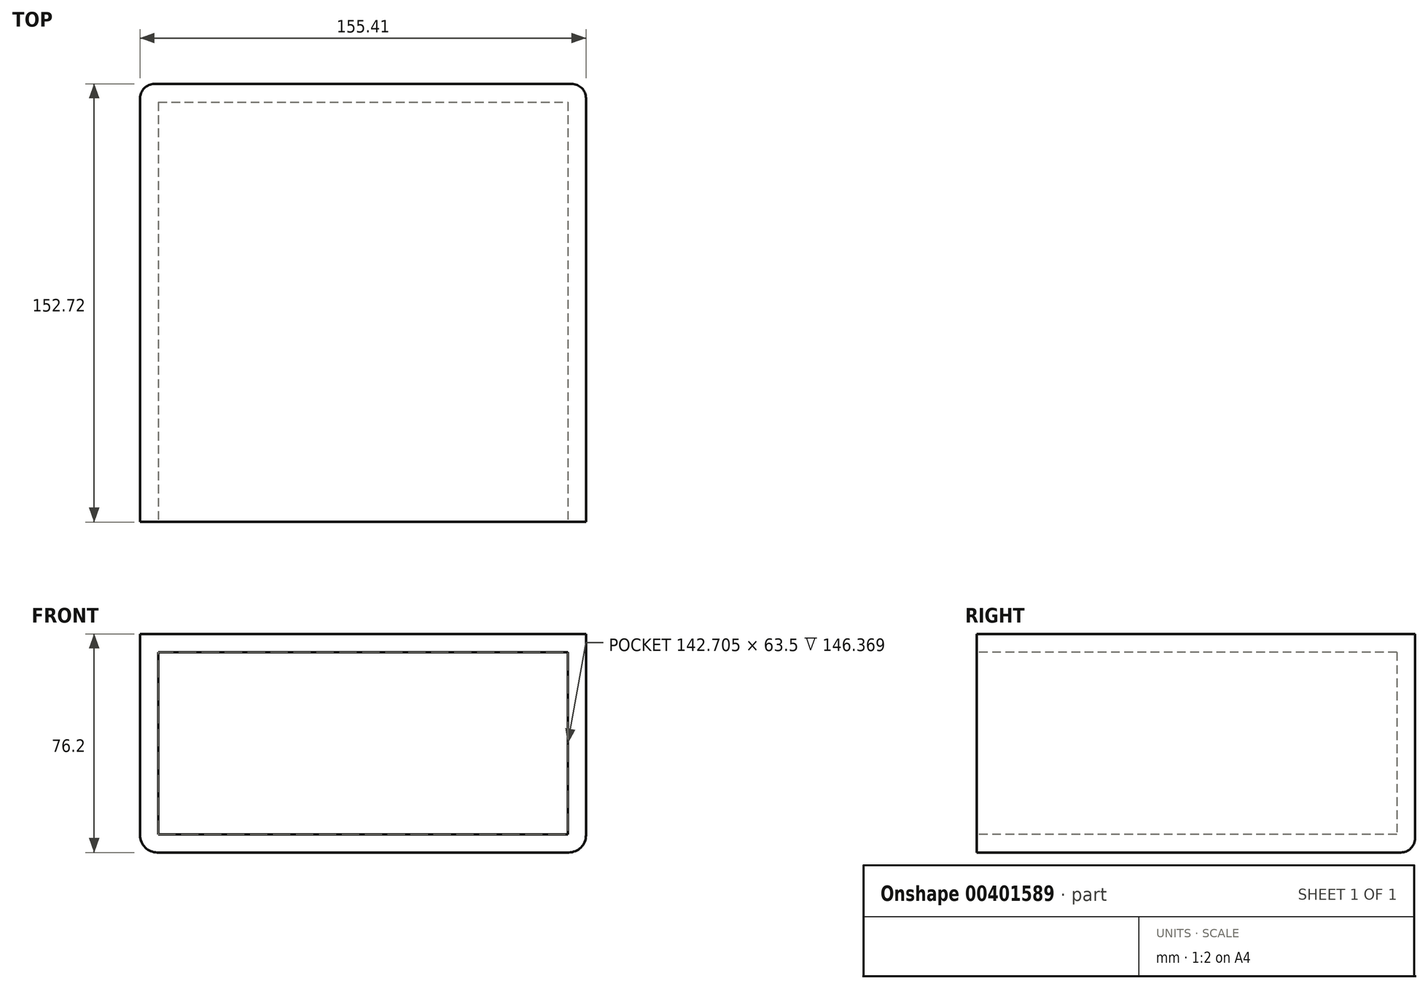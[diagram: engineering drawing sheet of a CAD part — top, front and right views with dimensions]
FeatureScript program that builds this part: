
annotation { "Feature Type Name" : "Feature", "Feature Type Description" : "" }
export const myFeature = defineFeature(function(context is Context, id is Id, definition is map)
    precondition{}
    {
        {
            var Q0;
            Q0=qCreatedBy(makeId("Top.planeOp"),FACE);
            var sketch = newSketch(context, id + "F0", { "sketchPlane" : qUnion([Q0])});
            skLineSegment(sketch, "E0.bottom", {"start": v(-79.4, 75.91) * mm, "end": v(76, 75.91) * mm});
            skLineSegment(sketch, "E0.top", {"start": v(-79.4, -76.8) * mm, "end": v(76, -76.8) * mm});
            skLineSegment(sketch, "E0.left", {"start": v(-79.4, 75.91) * mm, "end": v(-79.4, -76.8) * mm});
            skLineSegment(sketch, "E0.right", {"start": v(76, 75.91) * mm, "end": v(76, -76.8) * mm});
            skSolve(sketch);
        }
        {
            var Q0;
            Q0=makeQuery(id+"F0.imprint","IMPRINT",FACE,{"disambiguationData":[TD([[makeQuery(id+"F0.imprint","IMPRINT",EDGE,{"derivedFrom":sQuery(id+"F0.wireOp",EDGE,"E0.bottom")}),-1.0]])]});
            extrude(context, id + "F1", {"entities" : qUnion([Q0]), "depth" : 25.4 * mm});
        }
        {
            var Q0;
            Q0=makeQuery(id+"F1.opExtrude","CAP_FACE",FACE,{"disambiguationData":[OSD([sQuery(id+"F0.wireOp",EDGE,"E0.bottom"),sQuery(id+"F0.wireOp",EDGE,"E0.top"),sQuery(id+"F0.wireOp",EDGE,"E0.left"),sQuery(id+"F0.wireOp",EDGE,"E0.right")])],"isStart":false});
            extrude(context, id + "F2", {"entities" : qUnion([Q0]), "operationType" : NewBodyOperationType.ADD, "depth" : 25.4 * mm});
        }
        {
            var Q0;
            Q0=makeQuery(id+"F1.opExtrude","CAP_FACE",FACE,{"disambiguationData":[OSD([sQuery(id+"F0.wireOp",EDGE,"E0.bottom"),sQuery(id+"F0.wireOp",EDGE,"E0.top"),sQuery(id+"F0.wireOp",EDGE,"E0.left"),sQuery(id+"F0.wireOp",EDGE,"E0.right")])],"isStart":false});
            var Q1;
            Q1=makeQuery(id+"F1.opExtrude","CAP_FACE",FACE,{"disambiguationData":[OSD([sQuery(id+"F0.wireOp",EDGE,"E0.bottom"),sQuery(id+"F0.wireOp",EDGE,"E0.top"),sQuery(id+"F0.wireOp",EDGE,"E0.left"),sQuery(id+"F0.wireOp",EDGE,"E0.right")])],"isStart":true});
            extrude(context, id + "F3", {"entities" : qUnion([Q0, Q1]), "operationType" : NewBodyOperationType.ADD, "depth" : 25.4 * mm});
        }
        {
            var Q0;
            {var subQ0=sQuery(id+"F0.wireOp",EDGE,"E0.top");Q0=makeQuery(id+"F3.boolean.opBoolean","MERGE",FACE,{"derivedFrom":[makeQuery(id+"F1.opExtrude","SWEPT_FACE",FACE,{"disambiguationData":[OSD([subQ0])]}),makeQuery(id+"F3.opExtrude","SWEPT_FACE",FACE,{"disambiguationData":[OSD([subQ0]),TDD([makeQuery(id+"F1.opExtrude","CAP_EDGE",EDGE,{"disambiguationData":[OSD([subQ0])],"isStart":true})])]}),makeQuery(id+"F3.opExtrude","SWEPT_FACE",FACE,{"disambiguationData":[OSD([subQ0]),TDD([makeQuery(id+"F1.opExtrude","CAP_EDGE",EDGE,{"disambiguationData":[OSD([subQ0])],"isStart":false})])]})]});}
            shell(context, id + "F4", {"entities" : qUnion([Q0]), "thickness" : 6.35 * mm});
        }
        {
            var Q0;
            {var subQ0=sQuery(id+"F0.wireOp",EDGE,"E0.left");Q0=makeQuery(id+"F3.opExtrude","CAP_EDGE",EDGE,{"disambiguationData":[OSD([subQ0]),TDD([makeQuery(id+"F1.opExtrude","CAP_EDGE",EDGE,{"disambiguationData":[OSD([subQ0])],"isStart":false})])],"isStart":false});}
            var Q1;
            Q1=makeQuery(id+"F1.opExtrude","CAP_EDGE",EDGE,{"disambiguationData":[OSD([sQuery(id+"F0.wireOp",EDGE,"E0.left")])],"isStart":true});
            var Q2;
            {var subQ0=sQuery(id+"F0.wireOp",EDGE,"E0.right");Q2=makeQuery(id+"F3.opExtrude","CAP_EDGE",EDGE,{"disambiguationData":[OSD([subQ0]),TDD([makeQuery(id+"F1.opExtrude","CAP_EDGE",EDGE,{"disambiguationData":[OSD([subQ0])],"isStart":false})])],"isStart":false});}
            var Q3;
            Q3=makeQuery(id+"F1.opExtrude","CAP_EDGE",EDGE,{"disambiguationData":[OSD([sQuery(id+"F0.wireOp",EDGE,"E0.right")])],"isStart":true});
            fillet(context, id + "F5", {"entities" : qUnion([Q0, Q1, Q2, Q3]), "radius" : 6 * mm, "tangentPropagation" : true, "allowEdgeOverflow" : false});
        }
        {
            var Q0;
            {var subQ0=sQuery(id+"F0.wireOp",EDGE,"E0.bottom");Q0=makeQuery(id+"F3.opExtrude","CAP_EDGE",EDGE,{"disambiguationData":[OSD([subQ0]),TDD([makeQuery(id+"F1.opExtrude","CAP_EDGE",EDGE,{"disambiguationData":[OSD([subQ0])],"isStart":false})])],"isStart":false});}
            var Q1;
            {var subQ0=sQuery(id+"F0.wireOp",EDGE,"E0.left");var subQ1=sQuery(id+"F0.wireOp",EDGE,"E0.bottom");Q1=makeQuery(id+"F3.boolean.opBoolean","MERGE",EDGE,{"derivedFrom":[makeQuery(id+"F1.opExtrude","SWEPT_EDGE",EDGE,{"disambiguationData":[OSD([subQ1,subQ0])]}),makeQuery(id+"F3.opExtrude","SWEPT_EDGE",EDGE,{"disambiguationData":[OSD([subQ1,subQ0]),TDD([makeQuery(id+"F1.opExtrude","CAP_VERTEX",VERTEX,{"disambiguationData":[OSD([subQ1,subQ0])],"isStart":true})])]}),makeQuery(id+"F3.opExtrude","SWEPT_EDGE",EDGE,{"disambiguationData":[OSD([subQ1,subQ0]),TDD([makeQuery(id+"F1.opExtrude","CAP_VERTEX",VERTEX,{"disambiguationData":[OSD([subQ1,subQ0])],"isStart":false})])]})]});}
            var Q2;
            Q2=makeQuery(id+"F1.opExtrude","CAP_EDGE",EDGE,{"disambiguationData":[OSD([sQuery(id+"F0.wireOp",EDGE,"E0.bottom")])],"isStart":true});
            var Q3;
            {var subQ0=sQuery(id+"F0.wireOp",EDGE,"E0.right");var subQ1=sQuery(id+"F0.wireOp",EDGE,"E0.bottom");Q3=makeQuery(id+"F3.boolean.opBoolean","MERGE",EDGE,{"derivedFrom":[makeQuery(id+"F1.opExtrude","SWEPT_EDGE",EDGE,{"disambiguationData":[OSD([subQ1,subQ0])]}),makeQuery(id+"F3.opExtrude","SWEPT_EDGE",EDGE,{"disambiguationData":[OSD([subQ1,subQ0]),TDD([makeQuery(id+"F1.opExtrude","CAP_VERTEX",VERTEX,{"disambiguationData":[OSD([subQ1,subQ0])],"isStart":true})])]}),makeQuery(id+"F3.opExtrude","SWEPT_EDGE",EDGE,{"disambiguationData":[OSD([subQ1,subQ0]),TDD([makeQuery(id+"F1.opExtrude","CAP_VERTEX",VERTEX,{"disambiguationData":[OSD([subQ1,subQ0])],"isStart":false})])]})]});}
            fillet(context, id + "F6", {"entities" : qUnion([Q0, Q1, Q2, Q3]), "radius" : 5 * mm, "tangentPropagation" : true, "allowEdgeOverflow" : false});
        }
    });
